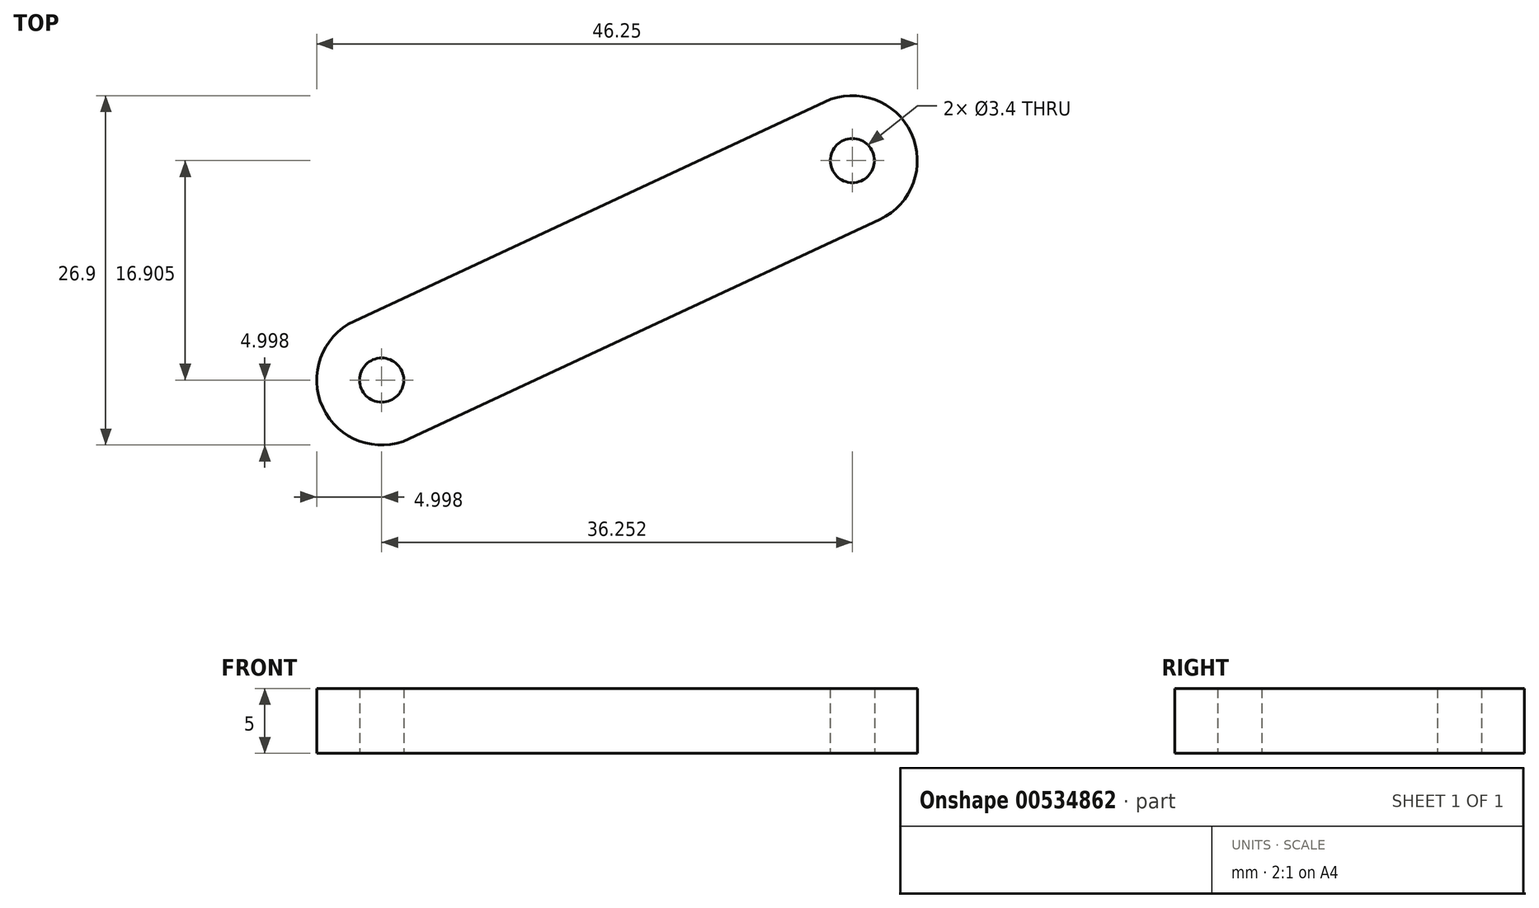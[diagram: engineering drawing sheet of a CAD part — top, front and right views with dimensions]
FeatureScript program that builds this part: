
annotation { "Feature Type Name" : "Feature", "Feature Type Description" : "" }
export const myFeature = defineFeature(function(context is Context, id is Id, definition is map)
    precondition{}
    {
        {
            var Q0;
            Q0=qCreatedBy(makeId("Top.planeOp"),FACE);
            var sketch = newSketch(context, id + "F0", { "sketchPlane" : qUnion([Q0])});
            skLineSegment(sketch, "E0.left", {"start": v(-5, 17.14) * mm, "end": v(-5, -22.86) * mm});
            skLineSegment(sketch, "E0.right", {"start": v(5, 17.14) * mm, "end": v(5, -22.86) * mm});
            skArc(sketch, "E1", {"start": v(-5, 17.14) * mm, "mid": v(0, 22.14) * mm, "end": v(5, 17.14) * mm});
            skArc(sketch, "E2", {"start": v(-5, -22.86) * mm, "mid": v(0, -27.86) * mm, "end": v(5, -22.86) * mm});
            skCircle(sketch, "E3", {"center": v(0, -22.86) * mm, "radius": 1.7 * mm});
            skCircle(sketch, "E4", {"center": v(0, 17.14) * mm, "radius": 1.7 * mm});
            skSolve(sketch);
        }
        {
            var Q0;
            Q0=qSketchRegion(id+"F0",true);
            extrude(context, id + "F1", {"entities" : qUnion([Q0]), "depth" : 5 * mm});
        }
        {
            var Q0;
            Q0=makeQuery(id+"F1.opExtrude","SWEPT_BODY",BODY,{"disambiguationData":[OSD([sQuery(id+"F0.wireOp",EDGE,"E0.left"),sQuery(id+"F0.wireOp",EDGE,"E0.right"),sQuery(id+"F0.wireOp",EDGE,"E1"),sQuery(id+"F0.wireOp",EDGE,"E2"),sQuery(id+"F0.wireOp",EDGE,"E3"),sQuery(id+"F0.wireOp",EDGE,"E4")])]});
            var Q1;
            Q1=makeQuery(id+"F1.opExtrude","CAP_EDGE",EDGE,{"disambiguationData":[OSD([sQuery(id+"F0.wireOp",EDGE,"E4")])],"isStart":false});
            transform(context, id + "F2", {"entities" : qUnion([Q0]), "transformType" : TransformType.ROTATION, "transformAxis" : qUnion([Q1]), "angle" : 65 * degree, "oppositeDirection" : true, "makeCopy" : false});
        }
    });
